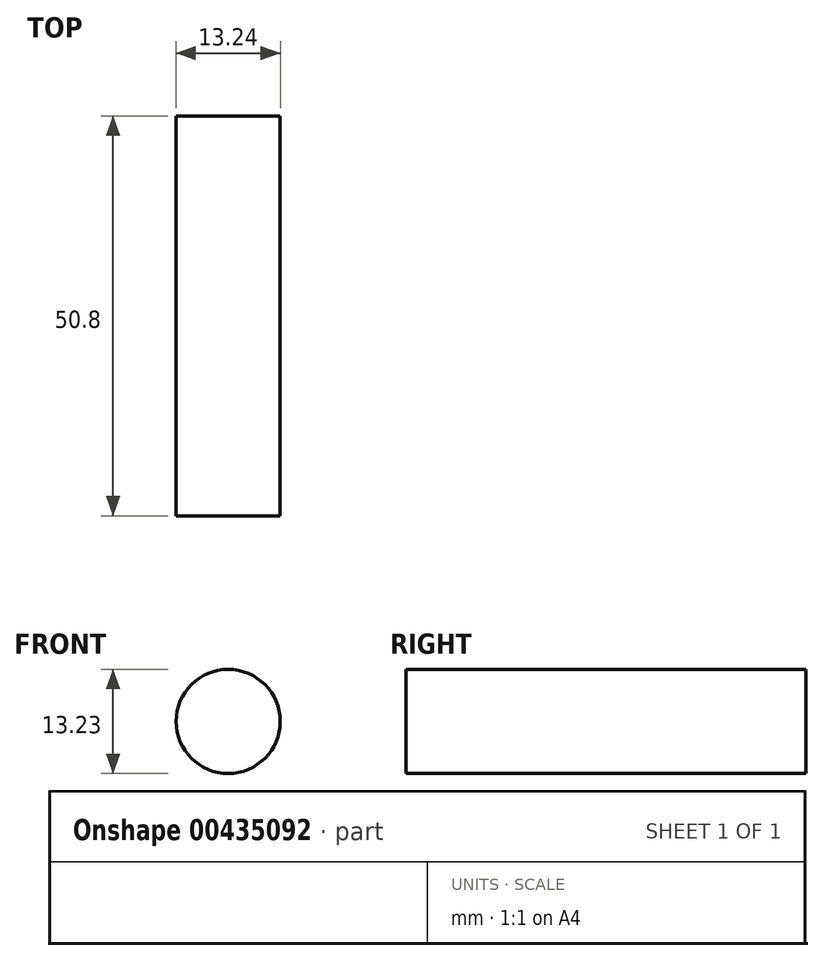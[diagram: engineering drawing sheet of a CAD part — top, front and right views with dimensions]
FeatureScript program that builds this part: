
annotation { "Feature Type Name" : "Feature", "Feature Type Description" : "" }
export const myFeature = defineFeature(function(context is Context, id is Id, definition is map)
    precondition{}
    {
        {
            var Q0;
            Q0=qCreatedBy(makeId("Front.planeOp"),FACE);
            var sketch = newSketch(context, id + "F0", { "sketchPlane" : qUnion([Q0])});
            skCircle(sketch, "E0", {"center": v(-44.5, 31.32) * mm, "radius": 6.62 * mm});
            skSolve(sketch);
        }
        {
            var Q0;
            Q0 = qSketchRegion(id + "F0", true);
            extrude(context, id + "F1", {"entities" : qUnion([Q0]), "depth" : 50.8 * mm});
        }
    });
